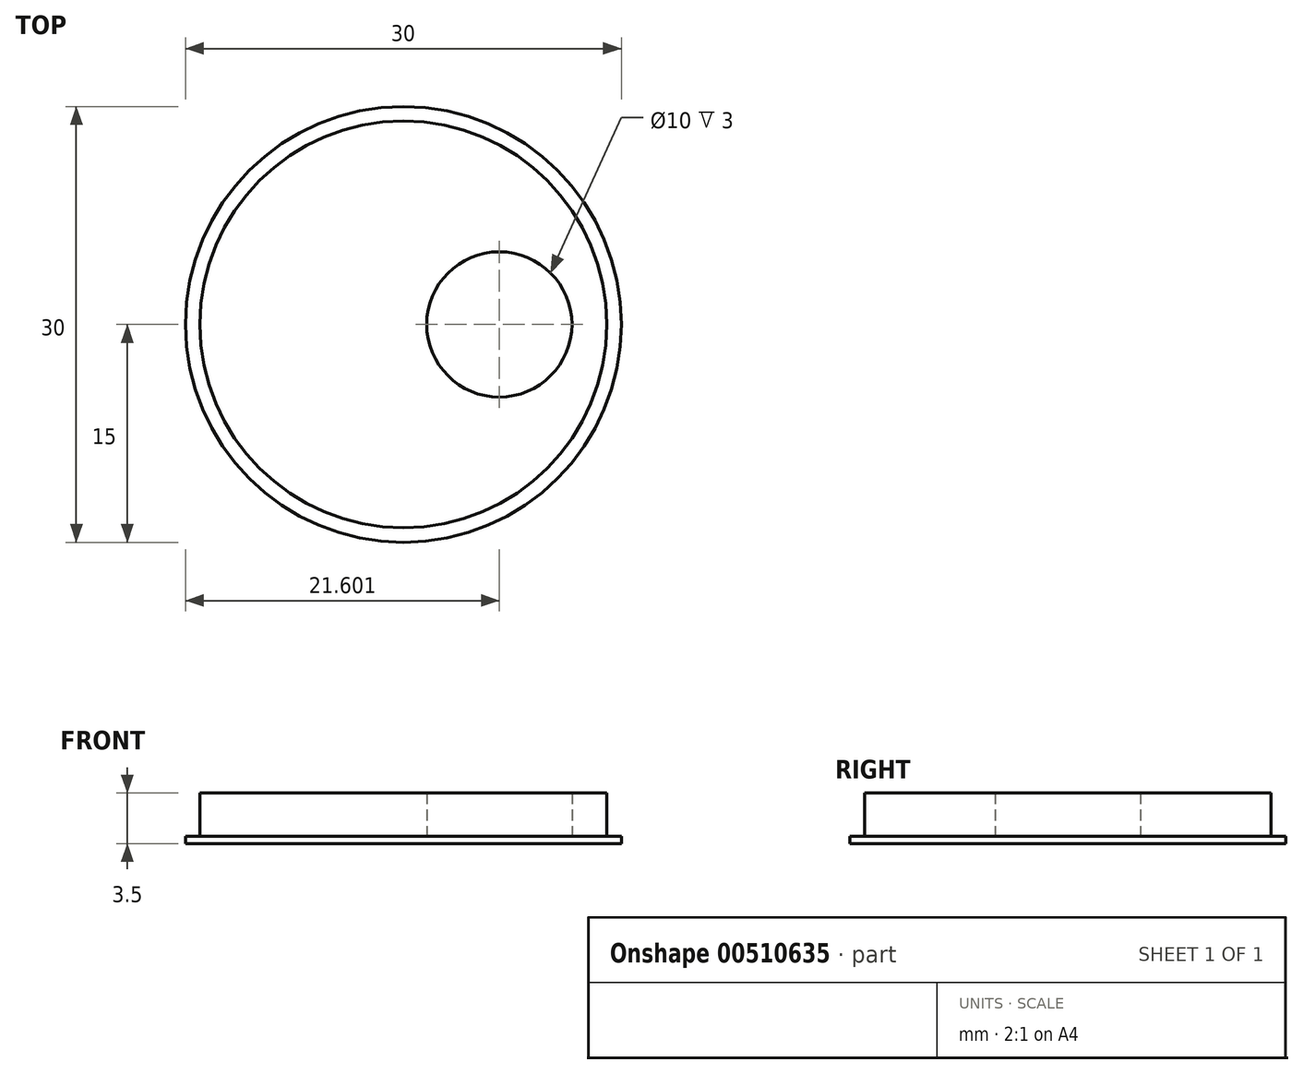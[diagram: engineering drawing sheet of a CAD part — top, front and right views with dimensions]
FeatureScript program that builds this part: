
annotation { "Feature Type Name" : "Feature", "Feature Type Description" : "" }
export const myFeature = defineFeature(function(context is Context, id is Id, definition is map)
    precondition{}
    {
        {
            var Q0;
            Q0=qCreatedBy(makeId("Top.planeOp"),FACE);
            var sketch = newSketch(context, id + "F0", { "sketchPlane" : qUnion([Q0])});
            skCircle(sketch, "E0", {"center": v(0, 0) * mm, "radius": 14 * mm});
            skCircle(sketch, "E1", {"center": v(6.6, 0) * mm, "radius": 5 * mm});
            skCircle(sketch, "E2", {"center": v(0, 0) * mm, "radius": 15 * mm});
            skSolve(sketch);
        }
        {
            var Q0;
            Q0=makeQuery(id+"F0.imprint","IMPRINT",FACE,{"disambiguationData":[TD([[makeQuery(id+"F0.imprint","IMPRINT",EDGE,{"derivedFrom":sQuery(id+"F0.wireOp",EDGE,"E0")}),1.0]])]});
            extrude(context, id + "F1", {"entities" : qUnion([Q0]), "depth" : 3 * mm});
        }
        {
            var Q0;
            Q0 = qSketchRegion(id + "F0", true);
            var Q1;
            Q1=makeQuery(id+"F1.opExtrude","CAP_FACE",FACE,{"disambiguationData":[OSD([sQuery(id+"F0.wireOp",EDGE,"E0"),sQuery(id+"F0.wireOp",EDGE,"E1")])],"isStart":false});
            var Q2;
            Q2=makeQuery(id+"F0.imprint","IMPRINT",FACE,{"disambiguationData":[TD([[makeQuery(id+"F0.imprint","IMPRINT",EDGE,{"derivedFrom":sQuery(id+"F0.wireOp",EDGE,"E1")}),1.0]])]});
            var Q3;
            Q3=makeQuery(id+"F0.imprint","IMPRINT",FACE,{"disambiguationData":[TD([[makeQuery(id+"F0.imprint","IMPRINT",EDGE,{"derivedFrom":sQuery(id+"F0.wireOp",EDGE,"E0")}),1.0]])]});
            extrude(context, id + "F2", {"entities" : qUnion([Q0, Q1, Q2, Q3]), "operationType" : NewBodyOperationType.ADD, "oppositeDirection" : true, "depth" : 0.5 * mm});
        }
    });
